# Revit family: Unterlegscheibe - DIN440 7 F -.pdf
name_source: partatom
category: Generic Models
revit_build: Autodesk Revit 2017 (Build: 20190508_0315(x64)
units: mm (PartAtom-declared; Revit-internal decimal feet)

## family parameters
Always vertical = Yes
Can host rebar = No
Cut with Voids When Loaded = No
Part Type = Normal
Room Calculation Point = No
Round Connector Dimension = Use Diameter
Shared = No
Work Plane-Based = No

## types (1)
- DIN440 7 F
    Article Type = DIN440 7 F
    Diameter = 7 mm  [stored 0.0229659 ft]
    Diameter 1 = 21 mm
    GTIN = 4012196479955
    Height = 2 mm  [stored 0.00656168 ft]
    Manufacturer = OBO BETTERMANN
    Manufacturer Art.No. = 6408702
    Material = hot dip galvanised
    URL = http://www.obo-bettermann.com

note: [stored X ft] marks values corroborated as IEEE doubles in the binary element streams (Revit-internal decimal feet)

## geometry (parser evidence)
native form markers: Sweep x3
no freeform markers — native parametric forms only
